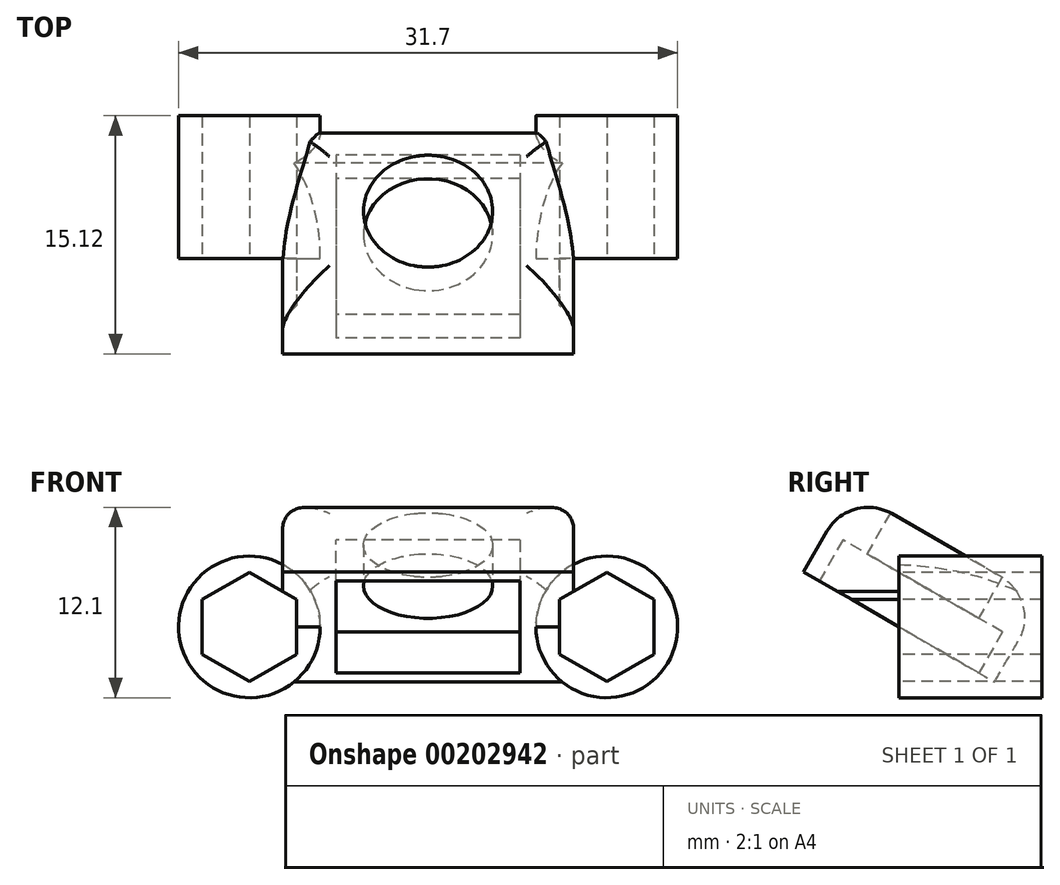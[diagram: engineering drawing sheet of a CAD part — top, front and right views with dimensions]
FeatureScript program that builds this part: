
annotation { "Feature Type Name" : "Feature", "Feature Type Description" : "" }
export const myFeature = defineFeature(function(context is Context, id is Id, definition is map)
    precondition{}
    {
        {
            var Q0;
            Q0=qCreatedBy(makeId("Top.planeOp"),FACE);
            var sketch = newSketch(context, id + "F0", { "sketchPlane" : qUnion([Q0])});
            skLineSegment(sketch, "E0.bottom", {"start": v(9.25, 7) * mm, "end": v(-9.25, 7) * mm});
            skLineSegment(sketch, "E0.top", {"start": v(9.25, -7) * mm, "end": v(-9.25, -7) * mm});
            skLineSegment(sketch, "E0.left", {"start": v(9.25, 7) * mm, "end": v(9.25, -7) * mm});
            skLineSegment(sketch, "E0.right", {"start": v(-9.25, 7) * mm, "end": v(-9.25, -7) * mm});
            skPoint(sketch, "E0.middle", {"position": v(0, 0) * mm});
            skLineSegment(sketch, "E1.bottom", {"start": v(5.85, 5.85) * mm, "end": v(-5.85, 5.85) * mm});
            skLineSegment(sketch, "E1.top", {"start": v(5.85, -5.85) * mm, "end": v(-5.85, -5.85) * mm});
            skLineSegment(sketch, "E1.left", {"start": v(5.85, 5.85) * mm, "end": v(5.85, -5.85) * mm});
            skLineSegment(sketch, "E1.right", {"start": v(-5.85, 5.85) * mm, "end": v(-5.85, -5.85) * mm});
            skCircle(sketch, "E2", {"center": v(0, 0) * mm, "radius": 4.1 * mm});
            skSolve(sketch);
        }
        {
            var Q0;
            Q0=makeQuery(id+"F0.imprint","IMPRINT",FACE,{"disambiguationData":[TD([[makeQuery(id+"F0.imprint","IMPRINT",EDGE,{"derivedFrom":sQuery(id+"F0.wireOp",EDGE,"E0.bottom")}),1.0]])]});
            var Q1;
            Q1=makeQuery(id+"F0.imprint","IMPRINT",FACE,{"disambiguationData":[TD([[makeQuery(id+"F0.imprint","IMPRINT",EDGE,{"derivedFrom":sQuery(id+"F0.wireOp",EDGE,"E1.bottom")}),1.0]])]});
            var Q2;
            Q2=makeQuery(id+"F0.imprint","IMPRINT",FACE,{"disambiguationData":[TD([[makeQuery(id+"F0.imprint","IMPRINT",EDGE,{"derivedFrom":sQuery(id+"F0.wireOp",EDGE,"E2")}),1.0]])]});
            extrude(context, id + "F1", {"entities" : qUnion([Q0, Q1, Q2]), "depth" : 6 * mm});
        }
        {
            var Q0;
            Q0=qCreatedBy(makeId("Top.planeOp"),FACE);
            var sketch = newSketch(context, id + "F2", { "sketchPlane" : qUnion([Q0])});
            skLineSegment(sketch, "E3", {"start": v(-15.14, 0) * mm, "end": v(14.33, 0) * mm});
            skSolve(sketch);
        }
        {
            var Q0;
            Q0=qCreatedBy(makeId("Front.planeOp"),FACE);
            var sketch = newSketch(context, id + "F3", { "sketchPlane" : qUnion([Q0])});
            skCircle(sketch, "E4.cCircle", {"center": v(-11.35, 0) * mm, "radius": 3 * mm, "construction": true});
            skLineSegment(sketch, "E4.0", {"start": v(-8.35, 1.73) * mm, "end": v(-8.35, -1.73) * mm});
            skLineSegment(sketch, "E4.1", {"start": v(-8.35, -1.73) * mm, "end": v(-11.35, -3.46) * mm});
            skLineSegment(sketch, "E4.2", {"start": v(-11.35, -3.46) * mm, "end": v(-14.35, -1.73) * mm});
            skLineSegment(sketch, "E4.3", {"start": v(-14.35, -1.73) * mm, "end": v(-14.35, 1.73) * mm});
            skLineSegment(sketch, "E4.4", {"start": v(-14.35, 1.73) * mm, "end": v(-11.35, 3.46) * mm});
            skLineSegment(sketch, "E4.5", {"start": v(-11.35, 3.46) * mm, "end": v(-8.35, 1.73) * mm});
            skPoint(sketch, "E4.0.midPoint", {"position": v(-8.35, 0) * mm});
            skCircle(sketch, "E5", {"center": v(-11.35, 0) * mm, "radius": 4.5 * mm});
            skCircle(sketch, "E6.1.0.0", {"center": v(11.35, 0) * mm, "radius": 4.5 * mm});
            skLineSegment(sketch, "E6.1.0.1", {"start": v(11.35, 3.46) * mm, "end": v(14.35, 1.73) * mm});
            skLineSegment(sketch, "E6.1.0.2", {"start": v(8.35, 1.73) * mm, "end": v(11.35, 3.46) * mm});
            skLineSegment(sketch, "E6.1.0.3", {"start": v(8.35, -1.73) * mm, "end": v(8.35, 1.73) * mm});
            skLineSegment(sketch, "E6.1.0.4", {"start": v(11.35, -3.46) * mm, "end": v(8.35, -1.73) * mm});
            skLineSegment(sketch, "E6.1.0.5", {"start": v(14.35, -1.73) * mm, "end": v(11.35, -3.46) * mm});
            skLineSegment(sketch, "E6.1.0.6", {"start": v(14.35, 1.73) * mm, "end": v(14.35, -1.73) * mm});
            skCircle(sketch, "E6.1.0.7", {"center": v(11.35, 0) * mm, "radius": 3 * mm, "construction": true});
            skPoint(sketch, "E6.1.0.8", {"position": v(14.35, 0) * mm});
            skCircle(sketch, "E6.2.0.0", {"center": v(34.05, 0) * mm, "radius": 4.5 * mm});
            skLineSegment(sketch, "E6.2.0.1", {"start": v(34.05, 3.46) * mm, "end": v(37.05, 1.73) * mm});
            skLineSegment(sketch, "E6.2.0.2", {"start": v(31.05, 1.73) * mm, "end": v(34.05, 3.46) * mm});
            skLineSegment(sketch, "E6.2.0.3", {"start": v(31.05, -1.73) * mm, "end": v(31.05, 1.73) * mm});
            skLineSegment(sketch, "E6.2.0.4", {"start": v(34.05, -3.46) * mm, "end": v(31.05, -1.73) * mm});
            skLineSegment(sketch, "E6.2.0.5", {"start": v(37.05, -1.73) * mm, "end": v(34.05, -3.46) * mm});
            skLineSegment(sketch, "E6.2.0.6", {"start": v(37.05, 1.73) * mm, "end": v(37.05, -1.73) * mm});
            skCircle(sketch, "E6.2.0.7", {"center": v(34.05, 0) * mm, "radius": 3 * mm, "construction": true});
            skPoint(sketch, "E6.2.0.8", {"position": v(37.05, 0) * mm});
            skLineSegment(sketch, "E6.direction1", {"start": v(-14.35, -1.73) * mm, "end": v(8.35, -1.73) * mm, "construction": true});
            skSolve(sketch);
        }
        {
            var Q0;
            Q0=makeQuery(id+"F0.imprint","IMPRINT",FACE,{"disambiguationData":[TD([[makeQuery(id+"F0.imprint","IMPRINT",EDGE,{"derivedFrom":sQuery(id+"F0.wireOp",EDGE,"E2")}),1.0]])]});
            extrude(context, id + "F4", {"entities" : qUnion([Q0]), "operationType" : NewBodyOperationType.REMOVE, "depth" : 6 * mm});
        }
        {
            var Q0;
            Q0=makeQuery(id+"F0.imprint","IMPRINT",FACE,{"disambiguationData":[TD([[makeQuery(id+"F0.imprint","IMPRINT",EDGE,{"derivedFrom":sQuery(id+"F0.wireOp",EDGE,"E1.bottom")}),1.0]])]});
            extrude(context, id + "F5", {"entities" : qUnion([Q0]), "operationType" : NewBodyOperationType.REMOVE, "depth" : 3 * mm});
        }
        {
            var Q0;
            Q0=makeQuery(id+"F1.opExtrude","SWEPT_BODY",BODY,{"disambiguationData":[OSD([sQuery(id+"F0.wireOp",EDGE,"E0.bottom"),sQuery(id+"F0.wireOp",EDGE,"E0.top"),sQuery(id+"F0.wireOp",EDGE,"E0.left"),sQuery(id+"F0.wireOp",EDGE,"E0.right")])]});
            var Q1;
            Q1=sQuery(id+"F2.wireOp",EDGE,"E3");
            transform(context, id + "F6", {"entities" : qUnion([Q0]), "transformType" : TransformType.ROTATION, "transformAxis" : qUnion([Q1]), "angle" : 30 * degree, "oppositeDirection" : true, "makeCopy" : false});
        }
        {
            var Q0;
            Q0=makeQuery(id+"F3.imprint","IMPRINT",FACE,{"disambiguationData":[TD([[makeQuery(id+"F3.imprint","IMPRINT",EDGE,{"derivedFrom":sQuery(id+"F3.wireOp",EDGE,"E4.0")}),1.0]])]});
            var Q1;
            Q1=makeQuery(id+"F3.imprint","IMPRINT",FACE,{"disambiguationData":[TD([[makeQuery(id+"F3.imprint","IMPRINT",EDGE,{"derivedFrom":sQuery(id+"F3.wireOp",EDGE,"E6.1.0.0")}),1.0]])]});
            var Q2;
            Q2=makeQuery(id+"F1.opExtrude","CAP_VERTEX",VERTEX,{"disambiguationData":[OSD([sQuery(id+"F0.wireOp",EDGE,"E0.bottom"),sQuery(id+"F0.wireOp",EDGE,"E0.right")])],"isStart":false});
            extrude(context, id + "F7", {"entities" : qUnion([Q0, Q1]), "operationType" : NewBodyOperationType.ADD, "endBound" : BoundingType.UP_TO_VERTEX, "oppositeDirection" : true, "endBoundEntityVertex" : qUnion([Q2]), "depth" : 9 * mm});
        }
        {
            var Q0;
            Q0=makeQuery(id+"F3.imprint","IMPRINT",FACE,{"disambiguationData":[TD([[makeQuery(id+"F3.imprint","IMPRINT",EDGE,{"derivedFrom":sQuery(id+"F3.wireOp",EDGE,"E6.1.0.1")}),-1.0]])]});
            var Q1;
            Q1=makeQuery(id+"F3.imprint","IMPRINT",FACE,{"disambiguationData":[TD([[makeQuery(id+"F3.imprint","IMPRINT",EDGE,{"derivedFrom":sQuery(id+"F3.wireOp",EDGE,"E4.0")}),-1.0]])]});
            extrude(context, id + "F8", {"entities" : qUnion([Q0, Q1]), "operationType" : NewBodyOperationType.REMOVE, "oppositeDirection" : true, "depth" : 25 * mm, "symmetric" : true});
        }
        {
            var Q0;
            {var subQ0=sQuery(id+"F0.wireOp",EDGE,"E0.right");var subQ1=sQuery(id+"F0.wireOp",EDGE,"E0.top");Q0=makeQuery(id+"F7.boolean.opBoolean","SPLIT",EDGE,{"disambiguationData":[TD([makeQuery(id+"F1.opExtrude","SWEPT_FACE",FACE,{"disambiguationData":[OSD([subQ1])]})])],"derivedFrom":makeQuery(id+"F1.opExtrude","CAP_EDGE",EDGE,{"disambiguationData":[OSD([subQ0])],"isStart":false})});}
            var Q1;
            Q1=makeQuery(id+"F1.opExtrude","CAP_EDGE",EDGE,{"disambiguationData":[OSD([sQuery(id+"F0.wireOp",EDGE,"E0.top")])],"isStart":false});
            var Q2;
            {var subQ0=sQuery(id+"F0.wireOp",EDGE,"E0.left");var subQ1=sQuery(id+"F0.wireOp",EDGE,"E0.top");Q2=makeQuery(id+"F7.boolean.opBoolean","SPLIT",EDGE,{"disambiguationData":[TD([makeQuery(id+"F1.opExtrude","SWEPT_FACE",FACE,{"disambiguationData":[OSD([subQ1])]})])],"derivedFrom":makeQuery(id+"F1.opExtrude","CAP_EDGE",EDGE,{"disambiguationData":[OSD([subQ0])],"isStart":false})});}
            fillet(context, id + "F9", {"entities" : qUnion([Q0, Q1, Q2]), "radius" : 3 * mm, "tangentPropagation" : true, "allowEdgeOverflow" : false});
        }
        {
            var Q0;
            {var subQ0=sQuery(id+"F3.wireOp",EDGE,"E5");var subQ1=sQuery(id+"F0.wireOp",EDGE,"E0.bottom");Q0=makeQuery(id+"F7.boolean.opBoolean","SPLIT",EDGE,{"disambiguationData":[TD([makeQuery(id+"F7.opExtrude","SWEPT_FACE",FACE,{"disambiguationData":[OSD([subQ0])]})])],"derivedFrom":makeQuery(id+"F1.opExtrude","CAP_EDGE",EDGE,{"disambiguationData":[OSD([subQ1])],"isStart":false})});}
            fillet(context, id + "F10", {"entities" : qUnion([Q0]), "radius" : 3 * mm, "tangentPropagation" : true, "allowEdgeOverflow" : false});
        }
    });
